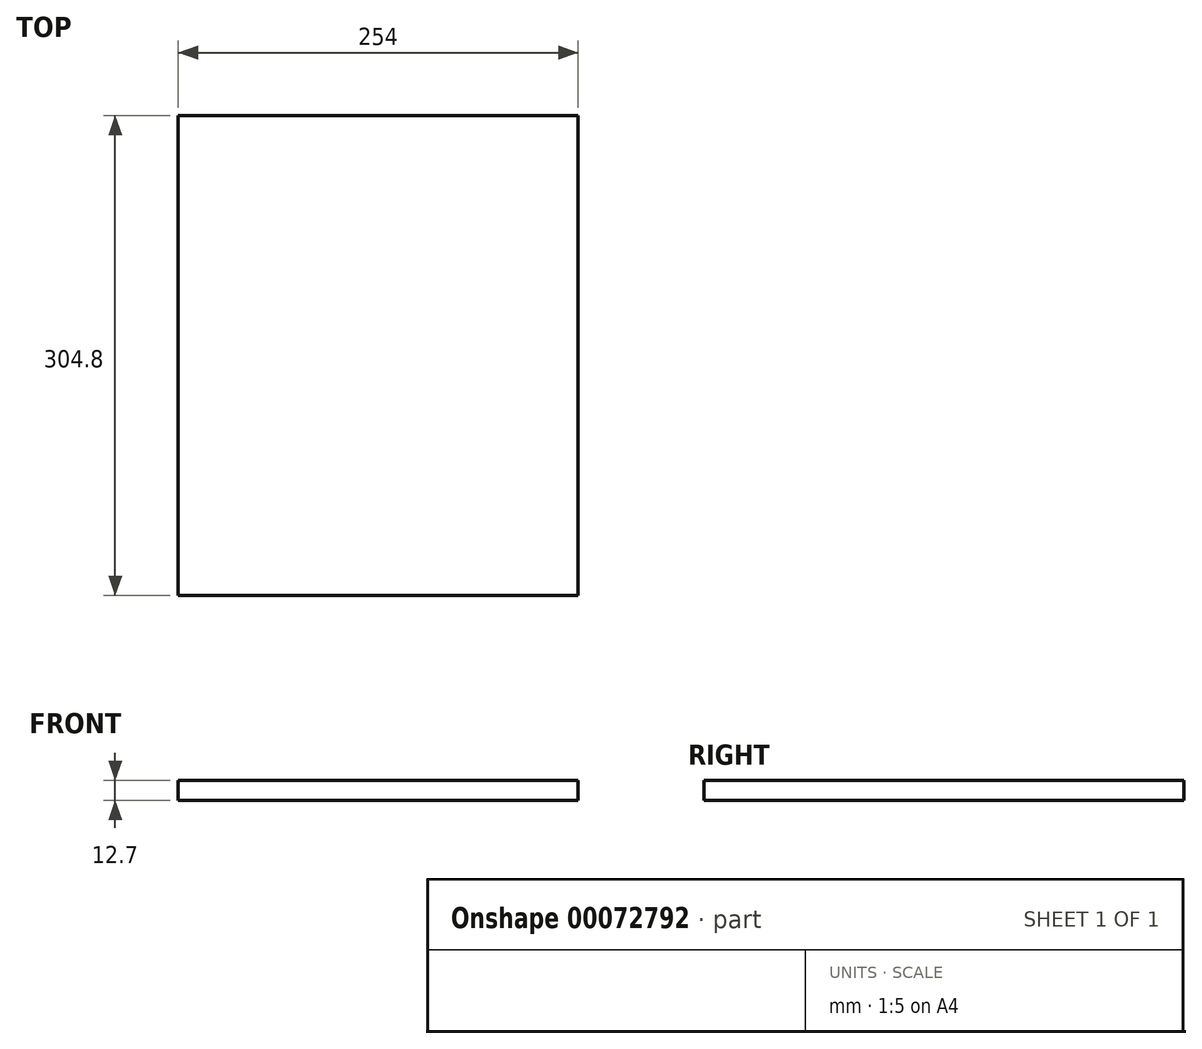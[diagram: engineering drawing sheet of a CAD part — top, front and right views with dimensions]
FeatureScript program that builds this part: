
annotation { "Feature Type Name" : "Feature", "Feature Type Description" : "" }
export const myFeature = defineFeature(function(context is Context, id is Id, definition is map)
    precondition{}
    {
        {
            var Q0;
            Q0=qCreatedBy(makeId("Top.planeOp"),FACE);
            var sketch = newSketch(context, id + "F0", { "sketchPlane" : qUnion([Q0])});
            skLineSegment(sketch, "E0.bottom", {"start": v(0, 0) * mm, "end": v(254, 0) * mm});
            skLineSegment(sketch, "E0.top", {"start": v(0, 304.8) * mm, "end": v(254, 304.8) * mm});
            skLineSegment(sketch, "E0.left", {"start": v(0, 0) * mm, "end": v(0, 304.8) * mm});
            skLineSegment(sketch, "E0.right", {"start": v(254, 0) * mm, "end": v(254, 304.8) * mm});
            skSolve(sketch);
        }
        {
            var Q0;
            Q0=makeQuery(id+"F0.imprint","IMPRINT",FACE,{"disambiguationData":[TD([[makeQuery(id+"F0.imprint","IMPRINT",EDGE,{"derivedFrom":sQuery(id+"F0.wireOp",EDGE,"E0.bottom")}),1.0]])]});
            extrude(context, id + "F1", {"entities" : qUnion([Q0]), "depth" : 12.7 * mm});
        }
    });
